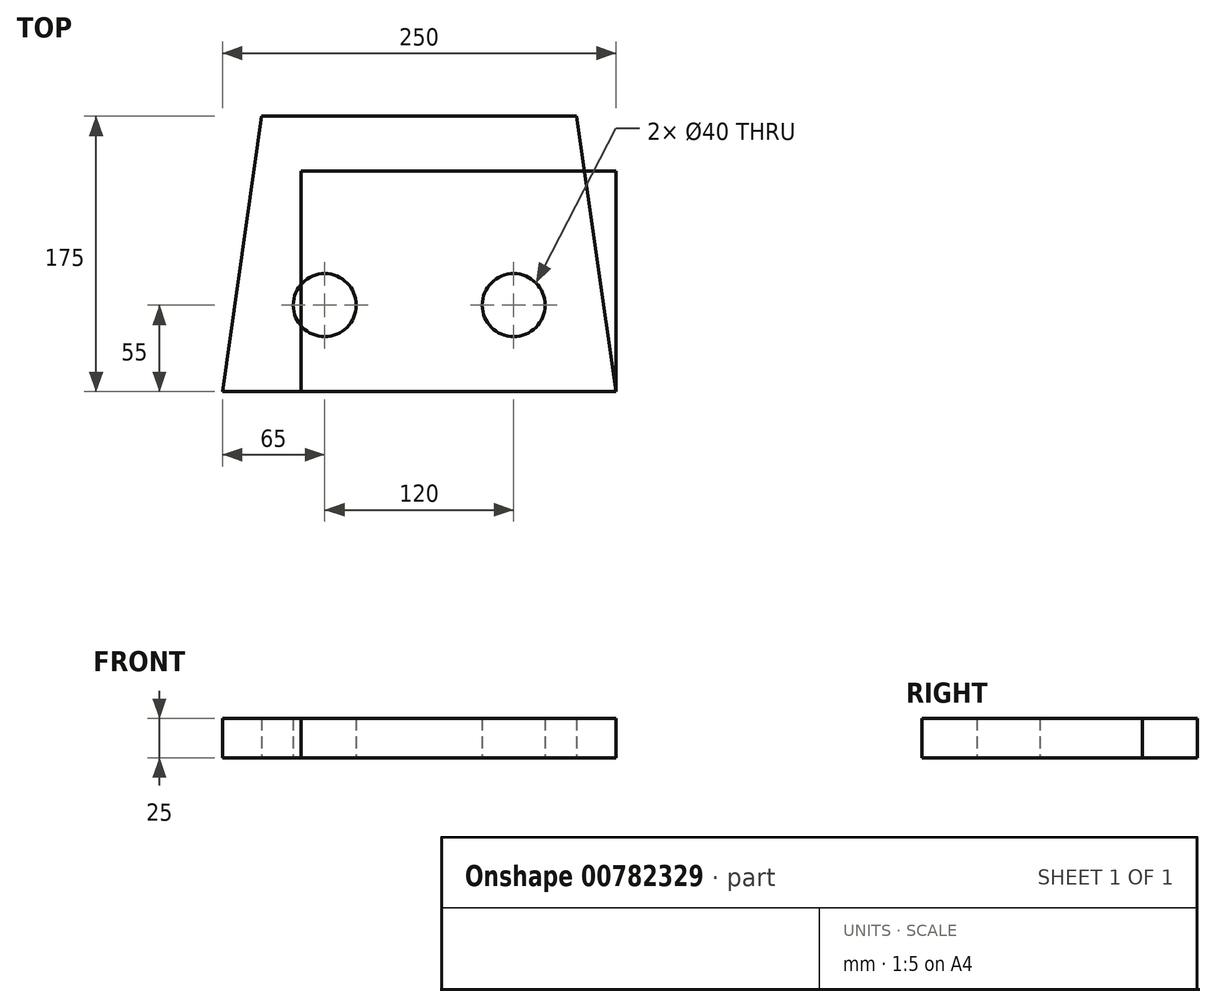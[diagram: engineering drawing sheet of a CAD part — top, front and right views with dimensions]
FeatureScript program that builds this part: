
annotation { "Feature Type Name" : "Feature", "Feature Type Description" : "" }
export const myFeature = defineFeature(function(context is Context, id is Id, definition is map)
    precondition{}
    {
        {
            var Q0;
            Q0=qCreatedBy(makeId("Top.planeOp"),FACE);
            var sketch = newSketch(context, id + "F0", { "sketchPlane" : qUnion([Q0])});
            skLineSegment(sketch, "E0.bottom", {"start": v(0, 0) * mm, "end": v(-200, 0) * mm});
            skLineSegment(sketch, "E0.top", {"start": v(0, 140) * mm, "end": v(-200, 140) * mm});
            skLineSegment(sketch, "E0.left", {"start": v(0, 0) * mm, "end": v(0, 140) * mm});
            skLineSegment(sketch, "E0.right", {"start": v(-200, 0) * mm, "end": v(-200, 140) * mm});
            skSolve(sketch);
        }
        {
            var Q0;
            Q0 = qSketchRegion(id + "F0", true);
            extrude(context, id + "F1", {"entities" : qUnion([Q0]), "depth" : 25 * mm, "offsetDistance" : 25 * mm});
        }
        {
            var Q0;
            Q0=qCreatedBy(makeId("Top.planeOp"),FACE);
            var sketch = newSketch(context, id + "F2", { "sketchPlane" : qUnion([Q0])});
            skLineSegment(sketch, "E1", {"start": v(0, 0) * mm, "end": v(-250, 0) * mm});
            skLineSegment(sketch, "E2", {"start": v(-250, 0) * mm, "end": v(-225, 175) * mm});
            skLineSegment(sketch, "E3", {"start": v(-225, 175) * mm, "end": v(-25, 175) * mm});
            skLineSegment(sketch, "E4", {"start": v(-25, 175) * mm, "end": v(0, 0) * mm});
            skCircle(sketch, "E5", {"center": v(-185, 55) * mm, "radius": 20 * mm});
            skCircle(sketch, "E6", {"center": v(-65, 55) * mm, "radius": 20 * mm});
            skPoint(sketch, "E7", {"position": v(-125, 0) * mm});
            skSolve(sketch);
        }
        {
            var Q0;
            Q0 = qSketchRegion(id + "F2", true);
            extrude(context, id + "F3", {"entities" : qUnion([Q0]), "depth" : 25 * mm, "offsetDistance" : 25 * mm});
        }
    });
